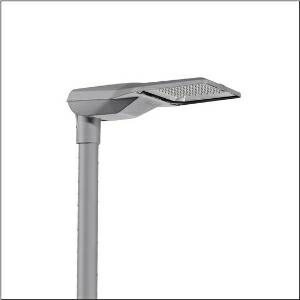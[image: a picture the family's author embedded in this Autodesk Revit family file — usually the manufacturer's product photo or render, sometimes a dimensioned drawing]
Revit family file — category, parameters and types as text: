
# Revit family: streetlight_sl_21_iq_midi___st1_0a_5xe3d61d08nb_4d1e
name_source: partatom
category: Lighting Fixtures
units: mm (PartAtom-declared; Revit-internal decimal feet)

## family parameters
Cut with Voids When Loaded = No
Host = Face
Light Source = No
Part Type = Normal
Room Calculation Point = No
Round Connector Dimension = Use Diameter
Shared = No

## types (1)
- --- (1 x LED, 20820 lm, 155.5 W, 2700K)
    Apparent Load = 155 VA
    CIE Flux Codes = 40 73 97 100 100
    Color Rendering = 70
    Color Temperature = 2700K
    Default Elevation = 1800 mm
    Description = Streetlight SL 21 iQ midi, mast luminaire, primary light control with lens, of PMMA, primary optical cover: cover, of toughened safety glass, transparent, light distribution: ST1.0a, light emission: direct distribution, primary light characteristic: asymmetric, installation type: post-top, side-entry, LED, High Power LED, rated luminous flux: 20.820lm, luminous efficacy: 134lm/W, light colour: 727, colour temperature: 2700K, control gear: iQ-Comfort, control: Auto-Match, Temp-Guard, Lumen-Switch, Night-Set, Smart-Wire, Light-Fading, Desk-Remote (wireless, voltage-free reading and setting of iQ features in the workshop via application-optimized NFC function/RFID function), optimised constant luminous flux control (CLO 2.0), pre-setting: linear dimming characteristic, mains connection: 230..240V, AC, 50/60Hz, start of lifetime: 156W, end of service life: 162W, reduction: 69W, luminaire housing, of diecast aluminium, powder-coated, SITECO metallic grey (DB 702S), corrosivity category C5 high according to DIN EN ISO 12944, please order mast flange separately, inclination adjustable: 0°, 5°, 10°, 15°, sealing non-destructively replaceable, multi-level sealing system, length: 644mm, width: 335mm, height: 110mm, mast flange for spigot size: 42mm (side-entry): 5XC10008XM4, 60/48mm (side-entry/post-top): 5XC10108XM2, 76/60mm (side-entry/post-top): 5XC10108XM1, mounting height: 4..8m, protection rating (complete): IP66, insulation class (complete): insulation class II (safety insulation), certification: CE, ENEC, ENEC+, VDE, impact resistance: IK10, permissible operating ambient temperature for outdoor applications: -40..+50°C, standard-compliant lighting for roads and squares, packaging unit: 1 piece

Light Distribution: ST1.0a
    Height = 111 mm
    Lamp = 1 x LED
    Lamp Light Flux = 20820 lm
    Lamp Power = 155.5 W
    Lamp count = 1
    Length = 644 mm
    Luminous efficacy = 134 lm/W
    Manufacturer = Siteco
    ModVariant = No
    Model = 5XE3D61D08NB
    Number of Poles = 1
    OnlyDefault = Yes
    Power Factor = 1
    Product Name = Streetlight SL 21 iQ midi | ST1.0a
    Product group = mast luminaire | pylon top
    ProductGroupID = 6100
    Protection Class = Protection class II
    Protection Degree = IP 66
    RLX_Detail_Level = 1
    RLX_Emergency_Light_Flux = 0 lm
    RLX_Emergency_Type = 0
    RLX_Emergency_Type_DB = No
    RlxData = <blob elided: 27233 chars, md5=730ecc56>
    Socket = socket
    Standby Power = 0 W
    System Light Flux = 20820 lm
    System Power = 155 W
    Type Comments = factory setting: luminous flux: 100 % | dim-lin: 254 | 823 mA
    Type Image = l_1004298.jpg
    URL = http://relux.com
    VarID = @adj_170207
    Voltage = 0 V
    Weight = 0.00 kg
    Width = 336 mm

## geometry (parser evidence)
native form markers: Blend x4, Sweep x10
no freeform markers — native parametric forms only
